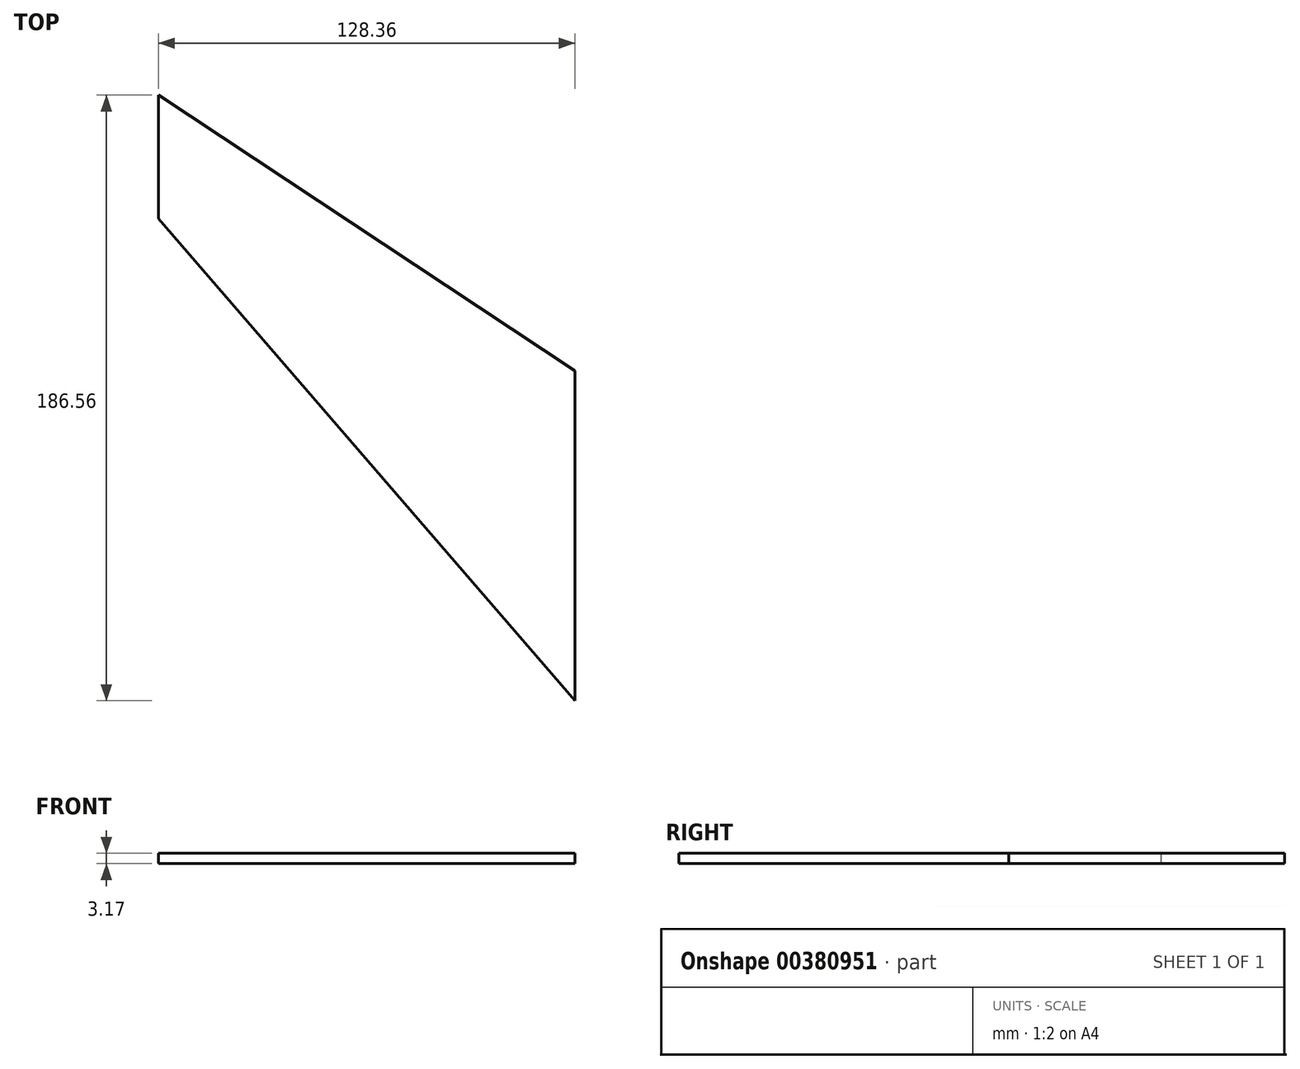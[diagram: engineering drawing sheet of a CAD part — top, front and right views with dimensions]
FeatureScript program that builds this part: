
annotation { "Feature Type Name" : "Feature", "Feature Type Description" : "" }
export const myFeature = defineFeature(function(context is Context, id is Id, definition is map)
    precondition{}
    {
        {
            var Q0;
            Q0=qCreatedBy(makeId("Top.planeOp"),FACE);
            var sketch = newSketch(context, id + "F0", { "sketchPlane" : qUnion([Q0])});
            skLineSegment(sketch, "E0", {"start": v(0, 0) * mm, "end": v(0, 101.6) * mm});
            skLineSegment(sketch, "E1", {"start": v(0, 101.6) * mm, "end": v(-128.36, 186.56) * mm});
            skLineSegment(sketch, "E2", {"start": v(-128.36, 186.56) * mm, "end": v(-128.36, 148.46) * mm});
            skLineSegment(sketch, "E3", {"start": v(-128.36, 84.96) * mm, "end": v(0, 0) * mm});
            skLineSegment(sketch, "E4", {"start": v(-128.36, 148.46) * mm, "end": v(0, 0) * mm});
            skSolve(sketch);
        }
        {
            var Q0;
            Q0=qSketchRegion(id+"F0",true);
            extrude(context, id + "F1", {"entities" : qUnion([Q0]), "depth" : 3.17 * mm});
        }
    });
